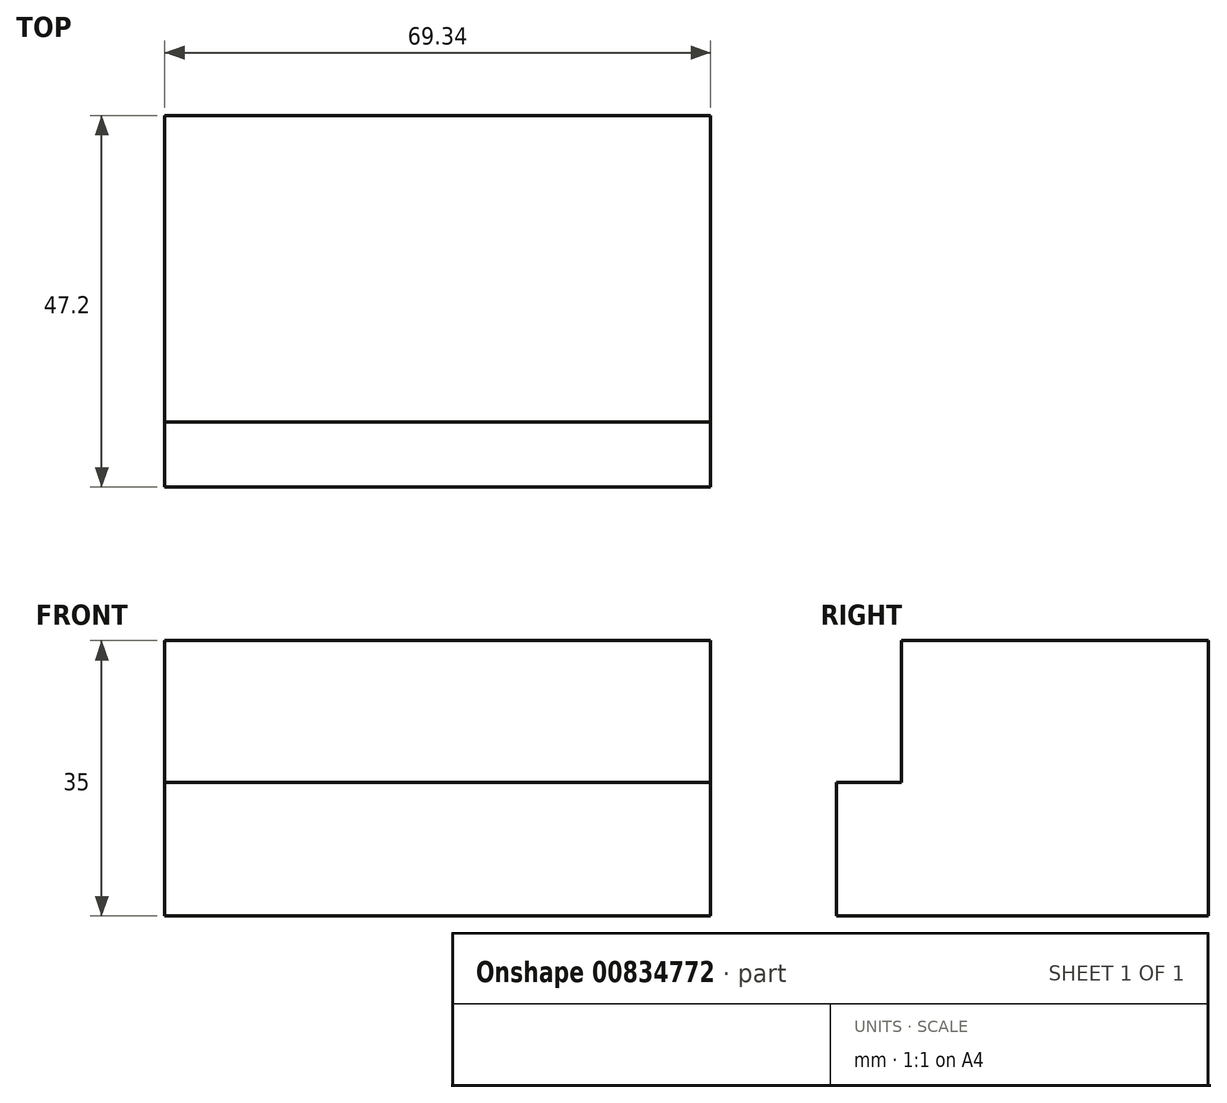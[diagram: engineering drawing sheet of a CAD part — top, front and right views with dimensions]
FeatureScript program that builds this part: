
annotation { "Feature Type Name" : "Feature", "Feature Type Description" : "" }
export const myFeature = defineFeature(function(context is Context, id is Id, definition is map)
    precondition{}
    {
        {
            var Q0;
            Q0=qCreatedBy(makeId("Top.planeOp"),FACE);
            var sketch = newSketch(context, id + "F0", { "sketchPlane" : qUnion([Q0])});
            skLineSegment(sketch, "E0.bottom", {"start": v(34.67, 23.6) * mm, "end": v(-34.67, 23.6) * mm});
            skLineSegment(sketch, "E0.top", {"start": v(34.67, -23.6) * mm, "end": v(-34.67, -23.6) * mm});
            skLineSegment(sketch, "E0.left", {"start": v(34.67, 23.6) * mm, "end": v(34.67, -23.6) * mm});
            skLineSegment(sketch, "E0.right", {"start": v(-34.67, 23.6) * mm, "end": v(-34.67, -23.6) * mm});
            skPoint(sketch, "E0.middle", {"position": v(0, 0) * mm});
            skSolve(sketch);
        }
        {
            var Q0;
            Q0=makeQuery(id+"F0.imprint","IMPRINT",FACE,{"disambiguationData":[TD([[makeQuery(id+"F0.imprint","IMPRINT",EDGE,{"derivedFrom":sQuery(id+"F0.wireOp",EDGE,"E0.bottom")}),1.0]])]});
            extrude(context, id + "F1", {"entities" : qUnion([Q0]), "depth" : 5 * mm, "offsetDistance" : 25 * mm});
        }
        {
            var Q0;
            Q0=makeQuery(id+"F1.opExtrude","CAP_FACE",FACE,{"disambiguationData":[OSD([sQuery(id+"F0.wireOp",EDGE,"E0.bottom"),sQuery(id+"F0.wireOp",EDGE,"E0.top"),sQuery(id+"F0.wireOp",EDGE,"E0.left"),sQuery(id+"F0.wireOp",EDGE,"E0.right")])],"isStart":true});
            extrude(context, id + "F2", {"entities" : qUnion([Q0]), "operationType" : NewBodyOperationType.ADD, "depth" : 5 * mm, "offsetDistance" : 25 * mm});
        }
        {
            var Q0;
            Q0=makeQuery(id+"F1.opExtrude","CAP_FACE",FACE,{"disambiguationData":[OSD([sQuery(id+"F0.wireOp",EDGE,"E0.bottom"),sQuery(id+"F0.wireOp",EDGE,"E0.top"),sQuery(id+"F0.wireOp",EDGE,"E0.left"),sQuery(id+"F0.wireOp",EDGE,"E0.right")])],"isStart":false});
            var sketch = newSketch(context, id + "F3", { "sketchPlane" : qUnion([Q0])});
            skLineSegment(sketch, "E1.bottom", {"start": v(-34.67, -23.6) * mm, "end": v(34.67, -23.6) * mm});
            skLineSegment(sketch, "E1.top", {"start": v(-34.67, -15.36) * mm, "end": v(34.67, -15.36) * mm});
            skLineSegment(sketch, "E1.left", {"start": v(-34.67, -23.6) * mm, "end": v(-34.67, -15.36) * mm});
            skLineSegment(sketch, "E1.right", {"start": v(34.67, -23.6) * mm, "end": v(34.67, -15.36) * mm});
            skSolve(sketch);
        }
        {
            var Q0;
            {var subQ0=sQuery(id+"F3.wireOp",EDGE,"E1.top");Q0=makeQuery(id+"F3.imprint","IMPRINT",FACE,{"disambiguationData":[TD([[makeQuery(id+"F3.imprint","IMPRINT",EDGE,{"derivedFrom":subQ0}),1.0]])]});}
            var sketch = newSketch(context, id + "F4", { "sketchPlane" : qUnion([Q0])});
            skSolve(sketch);
        }
        {
            var Q0;
            Q0=makeQuery(id+"F3.imprint","IMPRINT",FACE,{"disambiguationData":[TD([[makeQuery(id+"F3.imprint","IMPRINT",EDGE,{"derivedFrom":sQuery(id+"F3.wireOp",EDGE,"E1.bottom")}),-1.0]])]});
            extrude(context, id + "F5", {"entities" : qUnion([Q0]), "operationType" : NewBodyOperationType.ADD, "depth" : 7 * mm, "offsetDistance" : 25 * mm});
        }
        {
            var Q0;
            {var subQ0=sQuery(id+"F3.wireOp",EDGE,"E1.top");Q0=makeQuery(id+"F4.imprint","IMPRINT",FACE,{"disambiguationData":[TD([[makeQuery(id+"F4.imprint","IMPRINT",EDGE,{"derivedFrom":makeQuery(id+"F3.imprint","IMPRINT",EDGE,{"derivedFrom":subQ0})}),1.0]])]});}
            var sketch = newSketch(context, id + "F6", { "sketchPlane" : qUnion([Q0])});
            skSolve(sketch);
        }
        {
            var Q0;
            {var subQ0=sQuery(id+"F3.wireOp",EDGE,"E1.top");Q0=makeQuery(id+"F4.imprint","IMPRINT",FACE,{"disambiguationData":[TD([[makeQuery(id+"F4.imprint","IMPRINT",EDGE,{"derivedFrom":makeQuery(id+"F3.imprint","IMPRINT",EDGE,{"derivedFrom":subQ0})}),1.0]])]});}
            var Q1;
            {var subQ0=sQuery(id+"F3.wireOp",EDGE,"E1.top");Q1=makeQuery(id+"F6.imprint","IMPRINT",FACE,{"disambiguationData":[TD([[makeQuery(id+"F6.imprint","IMPRINT",EDGE,{"derivedFrom":makeQuery(id+"F4.imprint","IMPRINT",EDGE,{"derivedFrom":makeQuery(id+"F3.imprint","IMPRINT",EDGE,{"derivedFrom":subQ0})})}),1.0]])]});}
            extrude(context, id + "F7", {"entities" : qUnion([Q0, Q1]), "operationType" : NewBodyOperationType.ADD, "depth" : 25 * mm, "offsetDistance" : 25 * mm});
        }
    });
